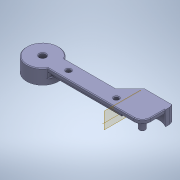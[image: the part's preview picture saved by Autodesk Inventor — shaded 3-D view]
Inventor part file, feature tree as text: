
AUTODESK INVENTOR PART (.ipt)
format: ipt  version: 2021 (Build 250183000, 183)  size: 400,384 bytes
history: native  units: mm
features: extrude x13, sketch x13, fillet x7, projected_geometry x4, chamfer x2, hole x1, plane x1, other x1
ambient origin geometry x8: Origin, YZ Plane, XZ Plane, XY Plane, X Axis, Y Axis, Z Axis, Center Point
bodies: Solid1 (feature_tree)
feature tree (42):
  extrude  "Extrusion1"  Depth=24.0mm
  extrude  "Extrusion2"  Depth=4.5mm
  extrude  "Extrusion3"  Depth=12.5mm
  extrude  "Extrusion4"  Depth=4.572mm
  hole  "Hole1"  [1 undecoded]
  extrude  "Extrusion5"  Depth=3.96875mm TaperAngle=0.0deg
  extrude  "Extrusion7"  Depth=18.0mm
  extrude  "Extrusion8"  Depth=3.969mm TaperAngle=0.0deg
  plane  "Work Plane1"
  other  "Work Axis1"
  extrude  "Extrusion9"  Depth=0.2mm TaperAngle=0.0deg
  extrude  "Extrusion11"  Depth=60.0mm
  extrude  "Extrusion12"  Depth=0.5mm
  extrude  "Extrusion14"  Depth=4.0mm TaperAngle=0.0deg
  chamfer  "Chamfer1"  Distance=10.0mm
  fillet  "Fillet2"  Radius=0.2mm
  fillet  "Fillet5"  Radius=0.5mm
  fillet  "Fillet6"  Radius=0.5mm
  fillet  "Fillet7"  Radius=0.5mm
  fillet  "Fillet9"  Radius=10.0mm
  fillet  "Fillet10"  Radius=0.5mm
  chamfer  "Chamfer3"  Distance=19.198622mm
  extrude  "Extrusion15"  TaperAngle=135.0deg  [1 undecoded]
  fillet  "Fillet11"  Radius=7.5mm
  extrude  "Extrusion16"  Depth=4.0mm
  sketch  "Sketch1"  dims[d0=4.572mm d1=24.0mm]
  sketch  "Sketch2"  dims[d2=75.0mm d3=4.5mm]
  sketch  "Sketch3"  dims[d4=18.0mm d5=12.5mm]
  sketch  "Sketch4"  dims[d6=3.0mm d7=0.0mm d8=4.572mm]
  projected_geometry  "Projected Loop1"
  sketch  "Sketch5"  dims[d9=25.0mm d10=3.96875mm d11=0.0mm]
  sketch  "Sketch6"  dims[d12=3.0mm d13=3.96875mm d14=0.0mm]
  sketch  "Sketch8"  dims[d15=4.269mm d16=0.0mm d17=18.0mm]
  sketch  "Sketch9"  dims[d18=18.0mm]
  projected_geometry  "Projected Loop2"
  sketch  "Sketch10"  dims[d19=3.25mm d20=6.0mm d21=4.0mm d22=2.0mm d23=90.0deg d24=8.0mm d25=20.594885mm d26=3.969mm d27=0.0mm]
  projected_geometry  "Projected Loop3"
  sketch  "Sketch13"  dims[d32=9.0mm d33=0.2mm d34=0.0mm]
  projected_geometry  "Projected Loop5"
  sketch  "Sketch15"  dims[d35=0.2mm d36=0.0mm d37=60.0mm]
  sketch  "Sketch16"  dims[d38=0.5mm d39=2.0mm d40=45.0deg d42=0.5mm]
  sketch  "Sketch17"  dims[d45=0.5mm d50=10.0mm d51=0.0mm d54=10.0mm d55=0.0mm d56=0.2mm d57=0.0mm d61=0.5mm d62=0.5mm d64=0.5mm d67=10.0mm d68=0.0mm d69=0.5mm d71=19.198622mm d72=135.0deg d73=7.5mm d74=15.0mm d75=0.25mm d76=2.0mm d77=45.0deg d78=3.5mm d79=0.0mm d80=0.5mm d81=4.0mm d82=0.0mm]
note: 2 required parameter values undecoded (feature->parameter linkage not recoverable at this tier; creation-order binding heuristic only, values carry confidence <= 0.55)
